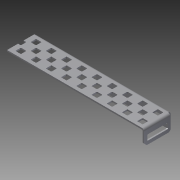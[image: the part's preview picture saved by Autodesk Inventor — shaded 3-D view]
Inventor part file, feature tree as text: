
AUTODESK INVENTOR PART (.ipt)
format: ipt  version: 2012 (Build 160160000, 160)  size: 885,760 bytes
history: native  units: in
note: dims shown in document units (in); Inventor stores cm internally (conversion verified against a paired STEP export)
features: other x1, imported_body x1, plane x1, split x1, extrude x1, fillet x1, sketch x1
ambient origin geometry x8: Origin, YZ Plane, XZ Plane, XY Plane, X Axis, Y Axis, Z Axis, Center Point
feature tree (7):
  parser-record x1  (decoder bookkeeping rows leaked as tree rows — omitted from the tree; the rows remain in map.json)
  imported_body  "Base1"
  plane  "Work Plane2"
  split  "Split1"
  extrude  "Extrusion1"  Depth=1.0in TaperAngle=0.0deg
  fillet  "Fillet1"  Radius=0.375in
  sketch  "Sketch1"  dims[d1=-8.0in d2=1.0in d3=0.0in d4=0.375in]
